# Revit family: 94008 163
name_source: partatom
category: Modelos genéricos
units: mm (PartAtom-declared; Revit-internal decimal feet)

## family parameters
Com base no plano de trabalho = Não
Compartilhado = Não
Corte com vazios quando carregada = Não
Cota do conector redondo = Utilizar diâmetro
Pode hospedar o vergalhão = Não
Ponto de cálculo do ambiente = Não
Sempre na vertical = Sim
Tipo de parte = Normal

## types (1)
- 94008 163
    Acabamento = Scotch Brite
    Acompanha o produto = 2 x válvula Ø 4 1/2 com escape
    Capacidade = 32 + 32 L
    Descrição = Cuba de sobrepor
    Dimensões = 890 x 460 x 212 mm (Profundidade)
    Elevação padrão = 0 mm  [stored 0 ft]
    Espessura = 1 mm
    Fabricante = Tramontina
    Manta adesiva anti-ruído = Sim
    Material predominante = Aço Inox
    Modelo = Cuba de sobrepor Quadrum 2C 40
    Obs. 1 Corte do Nicho = Dimensões de corte do tampo disponíveis para consulta no manual do produto, no site ou no gabarito de corte que acompanha com a peça
    Obs. 2 Corte do Nicho = Para instalação da cuba no sistema Flush, deve ser adquirido em conjunto o Kit Flush ref. 94532_117
    Obs. 3 Corte do Nicho = Nicho de corte para instalação da cuba no sistema Semi-Flush: 860 x 430 mm
    Raio interno da cuba = 12 mm
    Referência do produto = 94008/163
    Tipo de material = AISI 304
    URL do fabricante = global.tramontina.com
    URL do produto = https://global.tramontina.com
    URL dos arquivos BIM = tramontina.com.br/biblioteca

note: [stored X ft] marks values corroborated as IEEE doubles in the binary element streams (Revit-internal decimal feet)
